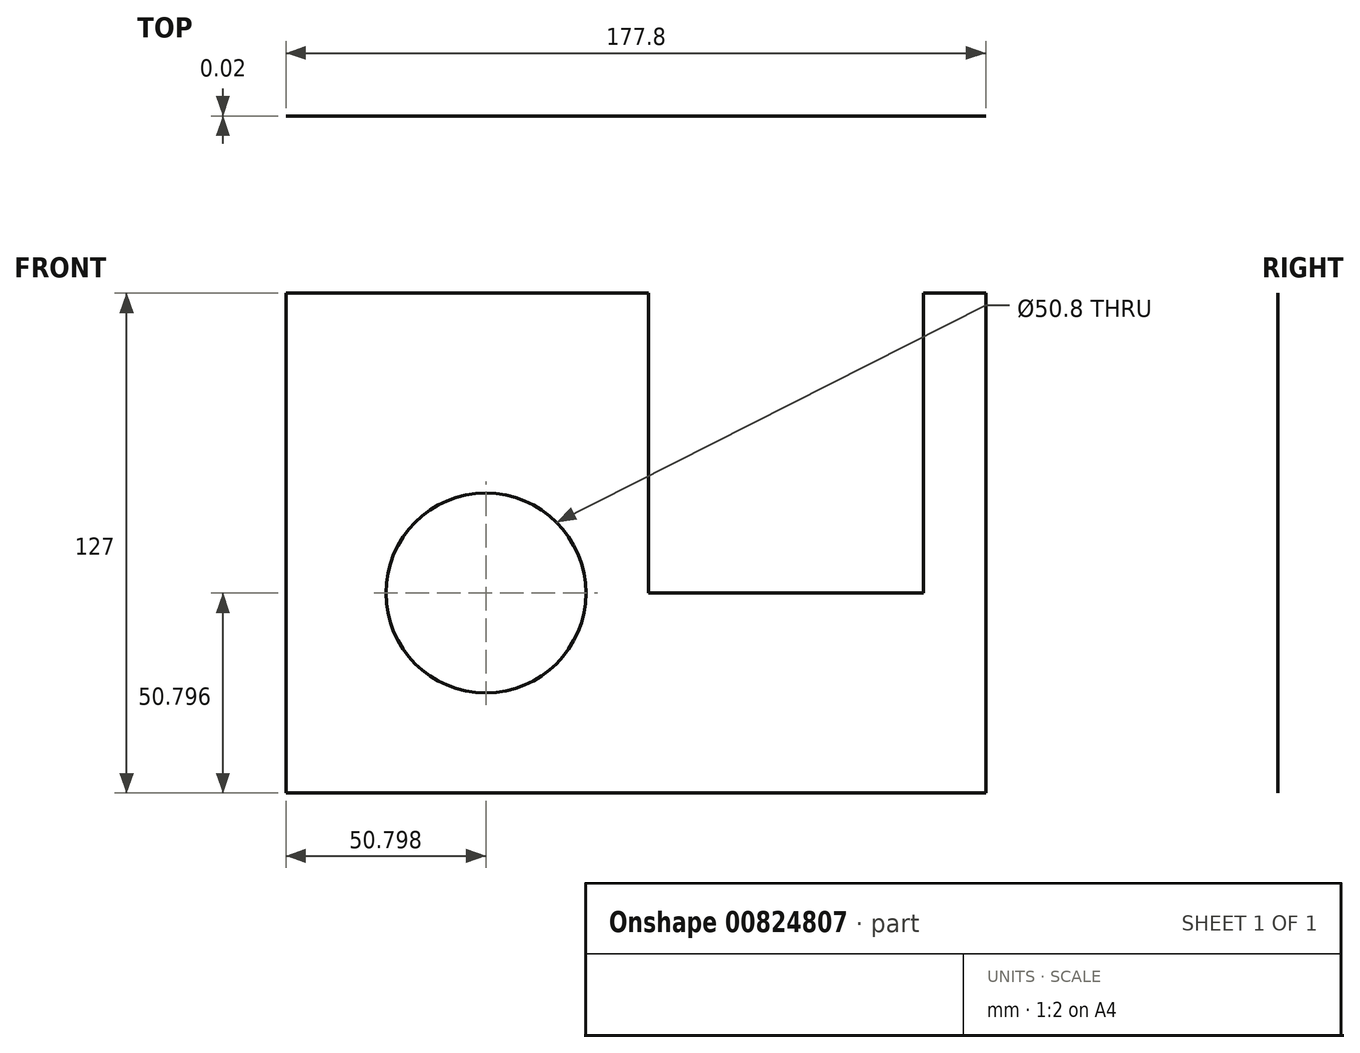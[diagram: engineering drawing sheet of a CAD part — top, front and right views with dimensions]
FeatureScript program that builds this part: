
annotation { "Feature Type Name" : "Feature", "Feature Type Description" : "" }
export const myFeature = defineFeature(function(context is Context, id is Id, definition is map)
    precondition{}
    {
        {
            var Q0;
            Q0=qCreatedBy(makeId("Front.planeOp"),FACE);
            var sketch = newSketch(context, id + "F0", { "sketchPlane" : qUnion([Q0])});
            skLineSegment(sketch, "E0", {"start": v(-96.02, 53.25) * mm, "end": v(-96.02, -73.75) * mm});
            skLineSegment(sketch, "E1", {"start": v(-96.02, 53.25) * mm, "end": v(-3.95, 53.25) * mm});
            skLineSegment(sketch, "E2", {"start": v(-3.95, 53.25) * mm, "end": v(-3.95, -22.95) * mm});
            skLineSegment(sketch, "E3", {"start": v(-3.95, -22.95) * mm, "end": v(65.9, -22.95) * mm});
            skLineSegment(sketch, "E4", {"start": v(65.9, -22.95) * mm, "end": v(65.9, 53.25) * mm});
            skLineSegment(sketch, "E5", {"start": v(65.9, 53.25) * mm, "end": v(81.78, 53.25) * mm});
            skLineSegment(sketch, "E6", {"start": v(-96.02, -73.75) * mm, "end": v(81.78, -73.75) * mm});
            skLineSegment(sketch, "E7", {"start": v(81.78, 53.25) * mm, "end": v(81.78, -73.75) * mm});
            skCircle(sketch, "E8", {"center": v(-45.22, -22.95) * mm, "radius": 25.4 * mm});
            skSolve(sketch);
        }
        {
            var Q0;
            Q0 = qSketchRegion(id + "F0", true);
            extrude(context, id + "F1", {"entities" : qUnion([Q0]), "depth" : 1 / 50.8 * mm, "offsetDistance" : 25 * mm});
        }
    });
